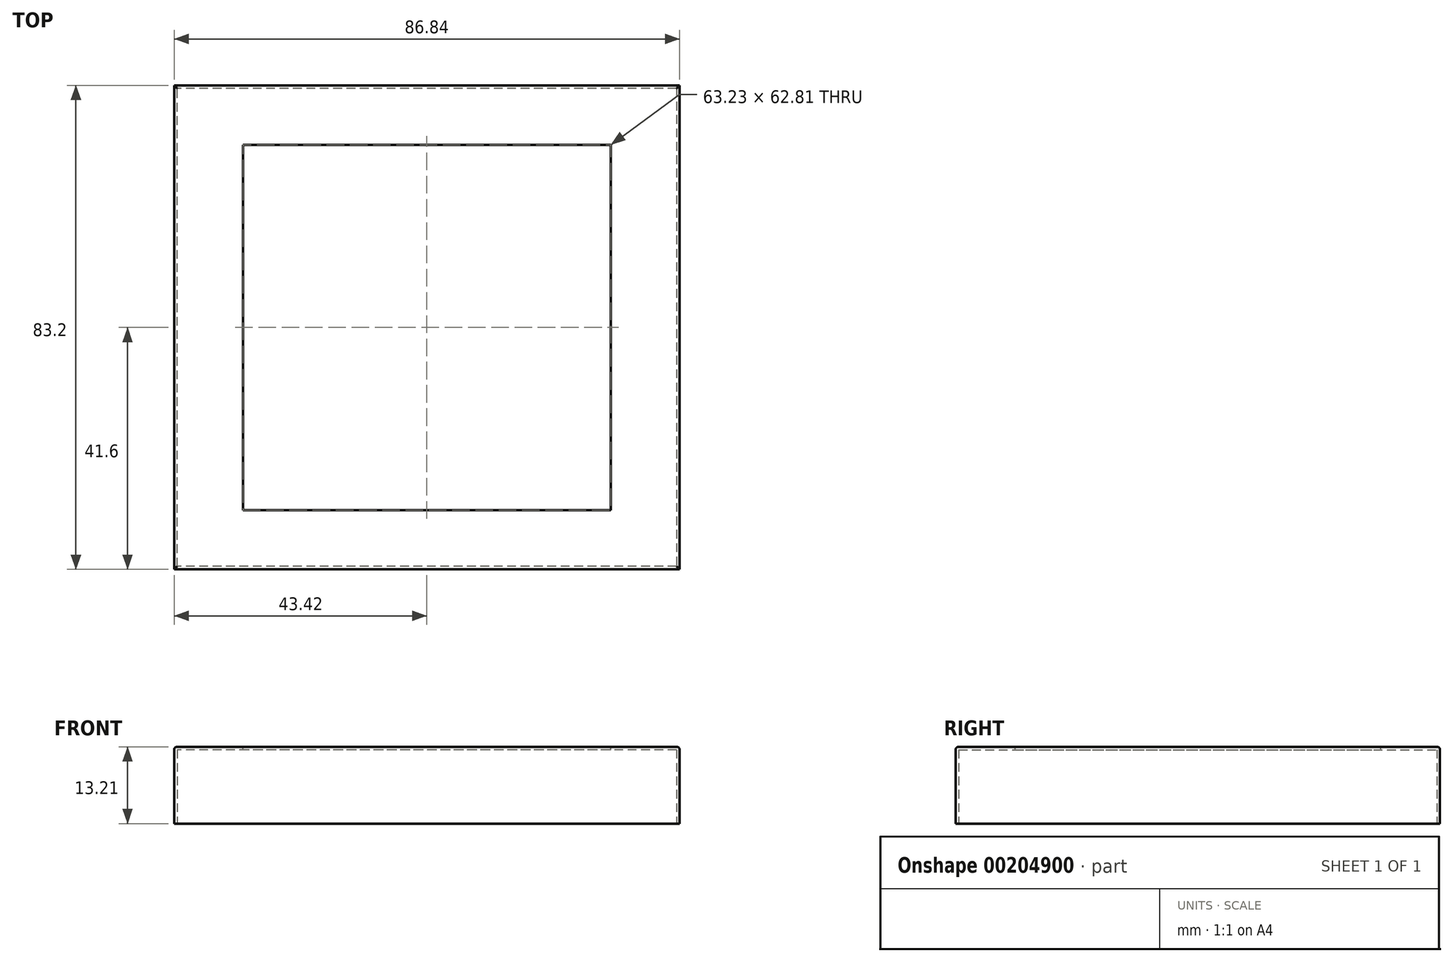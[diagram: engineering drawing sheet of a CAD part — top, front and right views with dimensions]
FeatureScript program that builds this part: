
annotation { "Feature Type Name" : "Feature", "Feature Type Description" : "" }
export const myFeature = defineFeature(function(context is Context, id is Id, definition is map)
    precondition{}
    {
        {
            var Q0;
            Q0=qCreatedBy(makeId("Top.planeOp"),FACE);
            var sketch = newSketch(context, id + "F0", { "sketchPlane" : qUnion([Q0])});
            skLineSegment(sketch, "E0.bottom", {"start": v(43.42, -41.6) * mm, "end": v(-43.42, -41.6) * mm});
            skLineSegment(sketch, "E0.top", {"start": v(43.42, 41.6) * mm, "end": v(-43.42, 41.6) * mm});
            skLineSegment(sketch, "E0.left", {"start": v(43.42, -41.6) * mm, "end": v(43.42, 41.6) * mm});
            skLineSegment(sketch, "E0.right", {"start": v(-43.42, -41.6) * mm, "end": v(-43.42, 41.6) * mm});
            skPoint(sketch, "E0.middle", {"position": v(0, 0) * mm});
            skSolve(sketch);
        }
        {
            var Q0;
            Q0 = qSketchRegion(id + "F0", true);
            extrude(context, id + "F1", {"entities" : qUnion([Q0]), "depth" : 13.2 * mm});
        }
        {
            var Q0;
            Q0=makeQuery(id+"F1.opExtrude","CAP_EDGE",EDGE,{"disambiguationData":[OSD([sQuery(id+"F0.wireOp",EDGE,"E0.bottom")])],"isStart":false});
            var Q1;
            Q1=makeQuery(id+"F1.opExtrude","CAP_EDGE",EDGE,{"disambiguationData":[OSD([sQuery(id+"F0.wireOp",EDGE,"E0.right")])],"isStart":false});
            var Q2;
            Q2=makeQuery(id+"F1.opExtrude","CAP_EDGE",EDGE,{"disambiguationData":[OSD([sQuery(id+"F0.wireOp",EDGE,"E0.top")])],"isStart":false});
            var Q3;
            Q3=makeQuery(id+"F1.opExtrude","CAP_EDGE",EDGE,{"disambiguationData":[OSD([sQuery(id+"F0.wireOp",EDGE,"E0.left")])],"isStart":false});
            fillet(context, id + "F2", {"entities" : qUnion([Q0, Q1, Q2, Q3]), "radius" : 0.5 * mm, "tangentPropagation" : true, "allowEdgeOverflow" : false});
        }
        {
            var Q0;
            Q0=makeQuery(id+"F1.opExtrude","CAP_FACE",FACE,{"disambiguationData":[OSD([sQuery(id+"F0.wireOp",EDGE,"E0.bottom"),sQuery(id+"F0.wireOp",EDGE,"E0.top"),sQuery(id+"F0.wireOp",EDGE,"E0.left"),sQuery(id+"F0.wireOp",EDGE,"E0.right")])],"isStart":true});
            shell(context, id + "F3", {"entities" : qUnion([Q0]), "thickness" : 0.5 * mm});
        }
        {
            var Q0;
            Q0=makeQuery(id+"F1.opExtrude","CAP_FACE",FACE,{"disambiguationData":[OSD([sQuery(id+"F0.wireOp",EDGE,"E0.bottom"),sQuery(id+"F0.wireOp",EDGE,"E0.top"),sQuery(id+"F0.wireOp",EDGE,"E0.left"),sQuery(id+"F0.wireOp",EDGE,"E0.right")])],"isStart":false});
            var sketch = newSketch(context, id + "F4", { "sketchPlane" : qUnion([Q0])});
            skLineSegment(sketch, "E1.bottom", {"start": v(31.61, -31.4) * mm, "end": v(-31.61, -31.4) * mm});
            skLineSegment(sketch, "E1.top", {"start": v(31.61, 31.4) * mm, "end": v(-31.61, 31.4) * mm});
            skLineSegment(sketch, "E1.left", {"start": v(31.61, -31.4) * mm, "end": v(31.61, 31.4) * mm});
            skLineSegment(sketch, "E1.right", {"start": v(-31.61, -31.4) * mm, "end": v(-31.61, 31.4) * mm});
            skPoint(sketch, "E1.middle", {"position": v(0, 0) * mm});
            skSolve(sketch);
        }
        {
            var Q0;
            Q0 = qSketchRegion(id + "F4", true);
            extrude(context, id + "F5", {"entities" : qUnion([Q0]), "operationType" : NewBodyOperationType.REMOVE, "oppositeDirection" : true, "depth" : 17.27 * mm});
        }
    });
